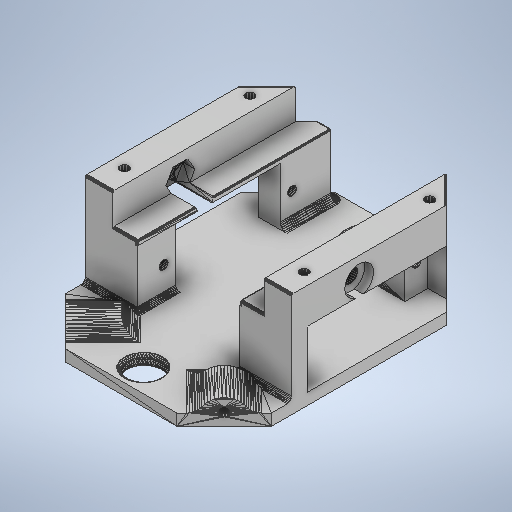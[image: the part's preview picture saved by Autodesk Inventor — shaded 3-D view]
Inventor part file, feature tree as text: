
AUTODESK INVENTOR PART (.ipt)
format: ipt  version: 2025.3 (Build 293356030, 356C)  size: 5,519,872 bytes
history: native  units: mm
features: other x3, sketch x1
ambient origin geometry x8: Origin, YZ Plane, XZ Plane, XY Plane, X Axis, Y Axis, Z Axis, Center Point
bodies: Solid1 (feature_tree)
feature tree (4):
  other  "chassis_a v1.ipt"
  other  "Solid1::chassis_a v1.ipt"
  other  "OperaciónIdentificador1"
  sketch  "Boceto1"  dims[d0=1.0mm]
